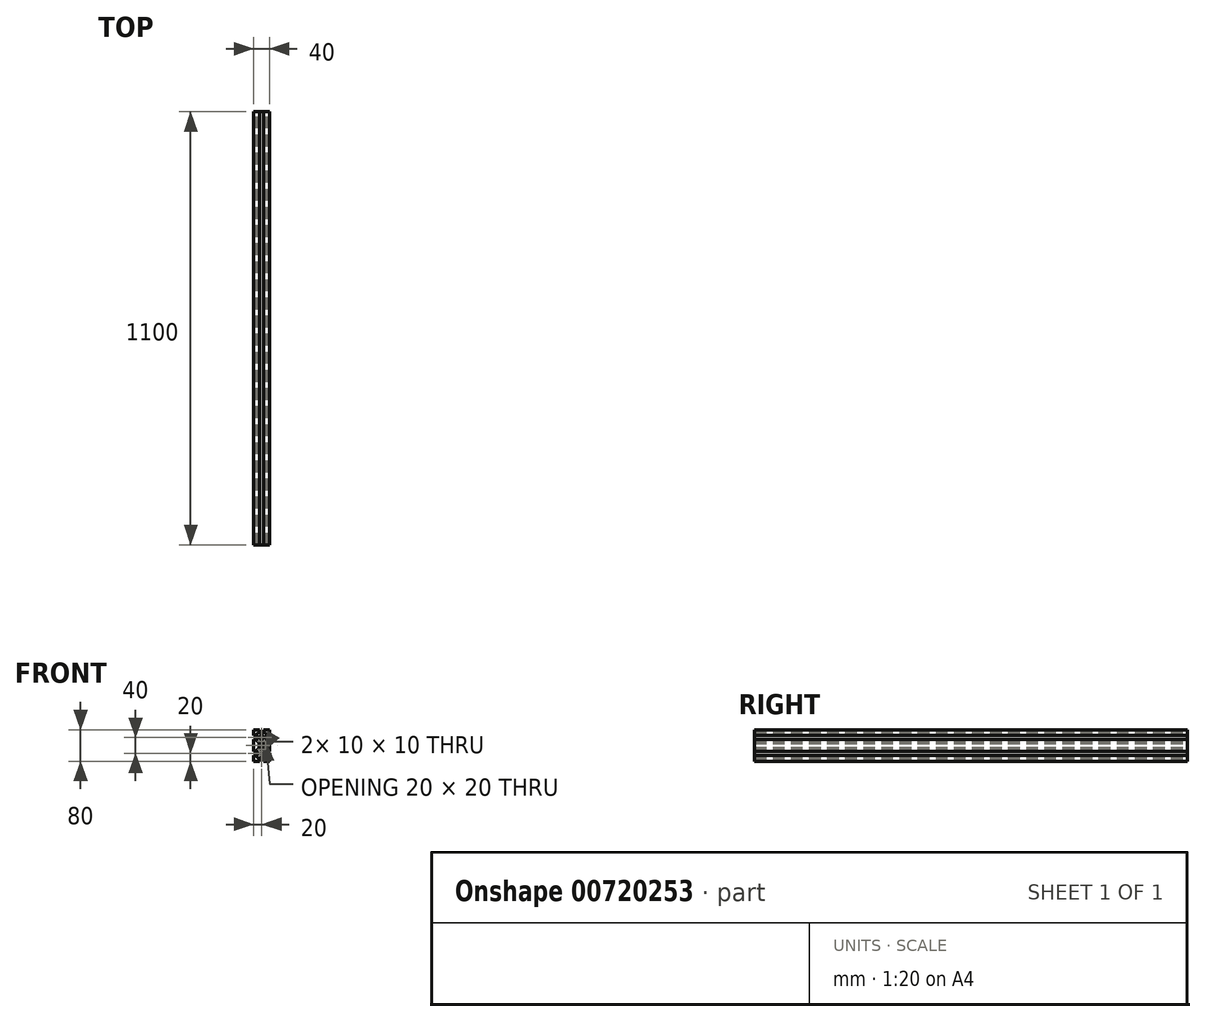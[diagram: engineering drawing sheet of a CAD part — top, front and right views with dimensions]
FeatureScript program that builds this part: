
annotation { "Feature Type Name" : "Feature", "Feature Type Description" : "" }
export const myFeature = defineFeature(function(context is Context, id is Id, definition is map)
    precondition{}
    {
        {
            var Q0;
            Q0=qCreatedBy(makeId("Front.planeOp"),FACE);
            var sketch = newSketch(context, id + "F0", { "sketchPlane" : qUnion([Q0])});
            skLineSegment(sketch, "E0.top", {"start": v(20, -20) * mm, "end": v(5, -20) * mm});
            skLineSegment(sketch, "E0.left", {"start": v(20, 20) * mm, "end": v(20, 5) * mm});
            skLineSegment(sketch, "E0.right", {"start": v(-20, 20) * mm, "end": v(-20, 5) * mm});
            skPoint(sketch, "E0.middle", {"position": v(0, 0) * mm});
            skLineSegment(sketch, "E1", {"start": v(0, 20) * mm, "end": v(0, -20) * mm, "construction": true});
            skLineSegment(sketch, "E2", {"start": v(-20, 0) * mm, "end": v(20, 0) * mm, "construction": true});
            skLineSegment(sketch, "E3", {"start": v(-20, 5) * mm, "end": v(-15, 5) * mm});
            skLineSegment(sketch, "E4", {"start": v(-20, -5) * mm, "end": v(-15, -5) * mm});
            skLineSegment(sketch, "E5", {"start": v(-5, 20) * mm, "end": v(-5, 15) * mm});
            skLineSegment(sketch, "E6", {"start": v(5, 20) * mm, "end": v(5, 15) * mm});
            skLineSegment(sketch, "E7", {"start": v(-10, 15) * mm, "end": v(-5, 15) * mm});
            skLineSegment(sketch, "E8", {"start": v(-10, -15) * mm, "end": v(-5, -15) * mm});
            skLineSegment(sketch, "E9", {"start": v(15, 10) * mm, "end": v(15, 5) * mm});
            skLineSegment(sketch, "E10", {"start": v(-15, 10) * mm, "end": v(-10, 5) * mm});
            skLineSegment(sketch, "E11", {"start": v(-10, 15) * mm, "end": v(-5, 10) * mm});
            skLineSegment(sketch, "E12", {"start": v(-15, -10) * mm, "end": v(-10, -5) * mm});
            skLineSegment(sketch, "E13", {"start": v(-10, -15) * mm, "end": v(-5, -10) * mm});
            skLineSegment(sketch, "E14.trimOffspring", {"start": v(20, -5) * mm, "end": v(20, -20) * mm});
            skLineSegment(sketch, "E15.trimOffspring", {"start": v(-20, -5) * mm, "end": v(-20, -20) * mm});
            skLineSegment(sketch, "E16.trimOffspring", {"start": v(-5, -20) * mm, "end": v(-20, -20) * mm});
            skLineSegment(sketch, "E17.trimOffspring", {"start": v(5, 15) * mm, "end": v(10, 15) * mm});
            skLineSegment(sketch, "E18.trimOffspring", {"start": v(-15, -5) * mm, "end": v(-15, -10) * mm});
            skLineSegment(sketch, "E19.trimOffspring", {"start": v(15, -5) * mm, "end": v(15, -10) * mm});
            skLineSegment(sketch, "E20.trimOffspring", {"start": v(5, -15) * mm, "end": v(10, -15) * mm});
            skLineSegment(sketch, "E21.trimOffspring", {"start": v(-5, 5) * mm, "end": v(-5, -5) * mm});
            skLineSegment(sketch, "E22.trimOffspring", {"start": v(5, 5) * mm, "end": v(5, -5) * mm});
            skLineSegment(sketch, "E23.trimOffspring", {"start": v(15, 5) * mm, "end": v(20, 5) * mm});
            skLineSegment(sketch, "E24.trimOffspring", {"start": v(15, -5) * mm, "end": v(20, -5) * mm});
            skLineSegment(sketch, "E25.trimOffspring", {"start": v(5, -15) * mm, "end": v(5, -20) * mm});
            skLineSegment(sketch, "E26.trimOffspring", {"start": v(-5, -15) * mm, "end": v(-5, -20) * mm});
            skLineSegment(sketch, "E27.trimOffspring", {"start": v(-5, -5) * mm, "end": v(5, -5) * mm});
            skLineSegment(sketch, "E28.trimOffspring", {"start": v(-5, 5) * mm, "end": v(5, 5) * mm});
            skLineSegment(sketch, "E29", {"start": v(10, 5) * mm, "end": v(10, -5) * mm});
            skLineSegment(sketch, "E30", {"start": v(-5, 10) * mm, "end": v(5, 10) * mm});
            skLineSegment(sketch, "E31", {"start": v(-10, 5) * mm, "end": v(-10, -5) * mm});
            skLineSegment(sketch, "E32", {"start": v(-5, -10) * mm, "end": v(5, -10) * mm});
            skLineSegment(sketch, "E33.trimOffspring", {"start": v(-15, 10) * mm, "end": v(-15, 5) * mm});
            skPoint(sketch, "E34.orphan", {"position": v(20, 15) * mm});
            skPoint(sketch, "E35.orphan", {"position": v(20, -15) * mm});
            skPoint(sketch, "E36.orphan", {"position": v(15, -20) * mm});
            skPoint(sketch, "E37.orphan", {"position": v(-15, -20) * mm});
            skLineSegment(sketch, "E38.trimOffspring", {"start": v(-5, 0) * mm, "end": v(0, -5) * mm});
            skLineSegment(sketch, "E39.trimOffspring", {"start": v(-5, 0) * mm, "end": v(0, 5) * mm});
            skLineSegment(sketch, "E40.trimOffspring", {"start": v(0, 5) * mm, "end": v(5, 0) * mm});
            skLineSegment(sketch, "E41.trimOffspring", {"start": v(5, 10) * mm, "end": v(10, 15) * mm});
            skLineSegment(sketch, "E42.trimOffspring", {"start": v(10, 5) * mm, "end": v(15, 10) * mm});
            skLineSegment(sketch, "E43.trimOffspring", {"start": v(10, -5) * mm, "end": v(15, -10) * mm});
            skLineSegment(sketch, "E44.trimOffspring", {"start": v(5, -10) * mm, "end": v(10, -15) * mm});
            skLineSegment(sketch, "E45.trimOffspring", {"start": v(0, -5) * mm, "end": v(5, 0) * mm});
            skLineSegment(sketch, "E46.bottom", {"start": v(20, 60) * mm, "end": v(5, 60) * mm});
            skLineSegment(sketch, "E46.left", {"start": v(20, 60) * mm, "end": v(20, 45) * mm});
            skLineSegment(sketch, "E46.right", {"start": v(-20, 60) * mm, "end": v(-20, 45) * mm});
            skPoint(sketch, "E46.middle", {"position": v(0, 40) * mm});
            skLineSegment(sketch, "E47", {"start": v(0, 60) * mm, "end": v(0, 20) * mm, "construction": true});
            skLineSegment(sketch, "E48", {"start": v(-20, 40) * mm, "end": v(20, 40) * mm, "construction": true});
            skLineSegment(sketch, "E49", {"start": v(-20, 45) * mm, "end": v(-15, 45) * mm});
            skLineSegment(sketch, "E50", {"start": v(-20, 35) * mm, "end": v(-15, 35) * mm});
            skLineSegment(sketch, "E51", {"start": v(-5, 60) * mm, "end": v(-5, 55) * mm});
            skLineSegment(sketch, "E52", {"start": v(5, 60) * mm, "end": v(5, 55) * mm});
            skLineSegment(sketch, "E53", {"start": v(-10, 55) * mm, "end": v(-5, 55) * mm});
            skLineSegment(sketch, "E54", {"start": v(-10, 25) * mm, "end": v(-5, 25) * mm});
            skLineSegment(sketch, "E55", {"start": v(15, 50) * mm, "end": v(15, 45) * mm});
            skLineSegment(sketch, "E56", {"start": v(-15, 50) * mm, "end": v(-10, 45) * mm});
            skLineSegment(sketch, "E57", {"start": v(-10, 55) * mm, "end": v(-5, 50) * mm});
            skLineSegment(sketch, "E58", {"start": v(-15, 30) * mm, "end": v(-10, 35) * mm});
            skLineSegment(sketch, "E59", {"start": v(-10, 25) * mm, "end": v(-5, 30) * mm});
            skLineSegment(sketch, "E60.trimOffspring", {"start": v(20, 35) * mm, "end": v(20, 20) * mm});
            skLineSegment(sketch, "E61.trimOffspring", {"start": v(-20, 35) * mm, "end": v(-20, 20) * mm});
            skLineSegment(sketch, "E62.trimOffspring", {"start": v(-5, 60) * mm, "end": v(-20, 60) * mm});
            skLineSegment(sketch, "E63.trimOffspring", {"start": v(5, 55) * mm, "end": v(10, 55) * mm});
            skLineSegment(sketch, "E64.trimOffspring", {"start": v(-15, 35) * mm, "end": v(-15, 30) * mm});
            skLineSegment(sketch, "E65.trimOffspring", {"start": v(15, 35) * mm, "end": v(15, 30) * mm});
            skLineSegment(sketch, "E66.trimOffspring", {"start": v(5, 25) * mm, "end": v(10, 25) * mm});
            skLineSegment(sketch, "E67.trimOffspring", {"start": v(-5, 45) * mm, "end": v(-5, 35) * mm});
            skLineSegment(sketch, "E68.trimOffspring", {"start": v(5, 45) * mm, "end": v(5, 35) * mm});
            skLineSegment(sketch, "E69.trimOffspring", {"start": v(15, 45) * mm, "end": v(20, 45) * mm});
            skLineSegment(sketch, "E70.trimOffspring", {"start": v(15, 35) * mm, "end": v(20, 35) * mm});
            skLineSegment(sketch, "E71.trimOffspring", {"start": v(5, 25) * mm, "end": v(5, 20) * mm});
            skLineSegment(sketch, "E72.trimOffspring", {"start": v(-5, 25) * mm, "end": v(-5, 20) * mm});
            skLineSegment(sketch, "E73.trimOffspring", {"start": v(-5, 35) * mm, "end": v(5, 35) * mm});
            skLineSegment(sketch, "E74.trimOffspring", {"start": v(-5, 45) * mm, "end": v(5, 45) * mm});
            skLineSegment(sketch, "E75", {"start": v(10, 45) * mm, "end": v(10, 35) * mm});
            skLineSegment(sketch, "E76", {"start": v(-5, 50) * mm, "end": v(5, 50) * mm});
            skLineSegment(sketch, "E77", {"start": v(-10, 45) * mm, "end": v(-10, 35) * mm});
            skLineSegment(sketch, "E78", {"start": v(-5, 30) * mm, "end": v(5, 30) * mm});
            skLineSegment(sketch, "E79.trimOffspring", {"start": v(-15, 50) * mm, "end": v(-15, 45) * mm});
            skPoint(sketch, "E80.orphan", {"position": v(20, 55) * mm});
            skPoint(sketch, "E81.orphan", {"position": v(20, 25) * mm});
            skPoint(sketch, "E82.orphan", {"position": v(15, 20) * mm});
            skLineSegment(sketch, "E83.trimOffspring", {"start": v(-5, 40) * mm, "end": v(0, 35) * mm});
            skLineSegment(sketch, "E84.trimOffspring", {"start": v(-5, 40) * mm, "end": v(0, 45) * mm});
            skLineSegment(sketch, "E85.trimOffspring", {"start": v(0, 45) * mm, "end": v(5, 40) * mm});
            skLineSegment(sketch, "E86.trimOffspring", {"start": v(5, 50) * mm, "end": v(10, 55) * mm});
            skLineSegment(sketch, "E87.trimOffspring", {"start": v(10, 45) * mm, "end": v(15, 50) * mm});
            skLineSegment(sketch, "E88.trimOffspring", {"start": v(10, 35) * mm, "end": v(15, 30) * mm});
            skLineSegment(sketch, "E89.trimOffspring", {"start": v(5, 30) * mm, "end": v(10, 25) * mm});
            skLineSegment(sketch, "E90.trimOffspring", {"start": v(0, 35) * mm, "end": v(5, 40) * mm});
            skSolve(sketch);
        }
        {
            var Q0;
            Q0=makeQuery(id+"F0.imprint","IMPRINT",FACE,{"disambiguationData":[TD([[makeQuery(id+"F0.imprint","IMPRINT",EDGE,{"derivedFrom":sQuery(id+"F0.wireOp",EDGE,"E0.top")}),-1.0]])]});
            extrude(context, id + "F1", {"entities" : qUnion([Q0]), "depth" : 1100 * mm, "offsetDistance" : 25 * mm});
        }
    });
